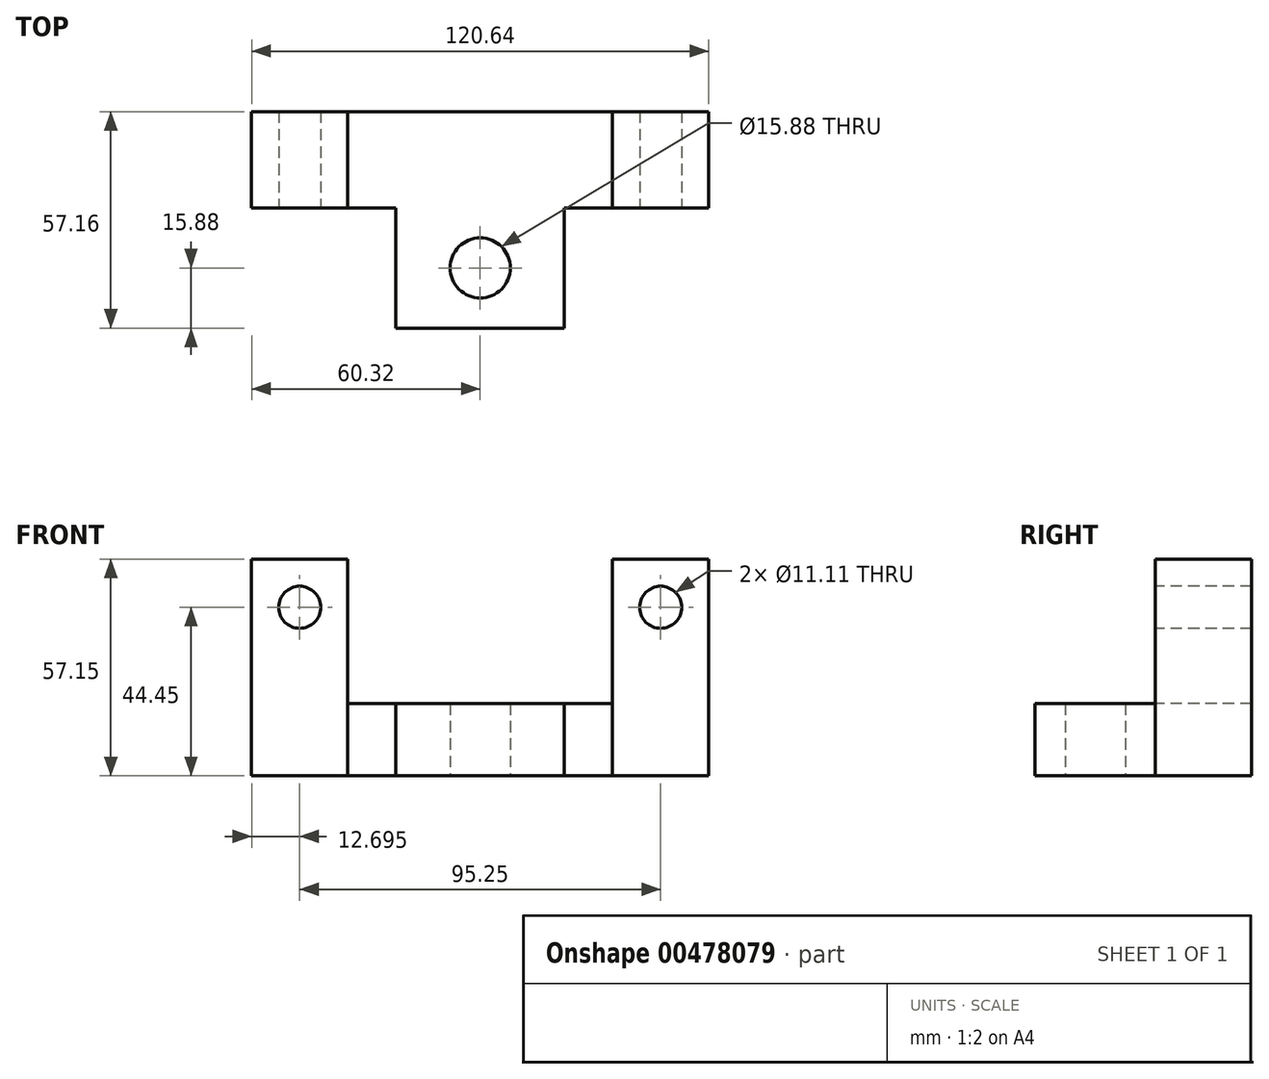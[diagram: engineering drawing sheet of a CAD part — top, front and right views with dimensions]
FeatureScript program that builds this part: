
annotation { "Feature Type Name" : "Feature", "Feature Type Description" : "" }
export const myFeature = defineFeature(function(context is Context, id is Id, definition is map)
    precondition{}
    {
        {
            var Q0;
            Q0=qCreatedBy(makeId("Top.planeOp"),FACE);
            var sketch = newSketch(context, id + "F0", { "sketchPlane" : qUnion([Q0])});
            skCircle(sketch, "E0", {"center": v(0, 0) * mm, "radius": 7.94 * mm});
            skLineSegment(sketch, "E1", {"start": v(-22.23, -15.88) * mm, "end": v(-22.23, 15.87) * mm});
            skLineSegment(sketch, "E2", {"start": v(-22.23, -15.88) * mm, "end": v(0, -15.88) * mm});
            skLineSegment(sketch, "E3", {"start": v(0, -15.88) * mm, "end": v(0, 15.87) * mm});
            skLineSegment(sketch, "E4", {"start": v(0, 15.87) * mm, "end": v(0, 41.28) * mm});
            skLineSegment(sketch, "E5", {"start": v(0, 41.28) * mm, "end": v(-34.93, 41.28) * mm});
            skLineSegment(sketch, "E6", {"start": v(-34.93, 41.28) * mm, "end": v(-34.93, 15.87) * mm});
            skLineSegment(sketch, "E7", {"start": v(-34.93, 15.87) * mm, "end": v(-22.23, 15.87) * mm});
            skLineSegment(sketch, "E8", {"start": v(-34.93, 41.28) * mm, "end": v(-60.32, 41.28) * mm});
            skLineSegment(sketch, "E9", {"start": v(-60.32, 41.27) * mm, "end": v(-60.32, 15.87) * mm});
            skLineSegment(sketch, "E10", {"start": v(-60.32, 15.87) * mm, "end": v(-34.93, 15.87) * mm});
            skLineSegment(sketch, "E11.MirrorCS", {"start": v(22.23, -15.88) * mm, "end": v(22.23, 15.87) * mm});
            skLineSegment(sketch, "E12.MirrorCS", {"start": v(60.32, 15.87) * mm, "end": v(34.93, 15.87) * mm});
            skLineSegment(sketch, "E13.MirrorCS", {"start": v(22.23, -15.88) * mm, "end": v(0, -15.88) * mm});
            skLineSegment(sketch, "E14.MirrorCS", {"start": v(60.32, 41.27) * mm, "end": v(60.32, 15.87) * mm});
            skLineSegment(sketch, "E15.MirrorCS", {"start": v(34.93, 15.87) * mm, "end": v(22.23, 15.87) * mm});
            skLineSegment(sketch, "E16.MirrorCS", {"start": v(34.93, 41.28) * mm, "end": v(60.32, 41.28) * mm});
            skLineSegment(sketch, "E17.MirrorCS", {"start": v(0, 41.28) * mm, "end": v(34.93, 41.28) * mm});
            skLineSegment(sketch, "E18.MirrorCS", {"start": v(34.93, 41.28) * mm, "end": v(34.93, 15.87) * mm});
            skSolve(sketch);
        }
        {
            var Q0;
            Q0=makeQuery(id+"F0.imprint","IMPRINT",FACE,{"disambiguationData":[TD([[makeQuery(id+"F0.imprint","IMPRINT",EDGE,{"derivedFrom":sQuery(id+"F0.wireOp",EDGE,"E8")}),1.0]])]});
            extrude(context, id + "F1", {"entities" : qUnion([Q0]), "depth" : 57.15 * mm});
        }
        {
            var Q0;
            Q0=makeQuery(id+"F0.imprint","IMPRINT",FACE,{"disambiguationData":[TD([[makeQuery(id+"F0.imprint","IMPRINT",EDGE,{"derivedFrom":sQuery(id+"F0.wireOp",EDGE,"E12.MirrorCS")}),-1.0]])]});
            extrude(context, id + "F2", {"entities" : qUnion([Q0]), "depth" : 57.15 * mm});
        }
        {
            var Q0;
            Q0=makeQuery(id+"F0.imprint","IMPRINT",FACE,{"disambiguationData":[TD([[makeQuery(id+"F0.imprint","IMPRINT",EDGE,{"derivedFrom":sQuery(id+"F0.wireOp",EDGE,"E1")}),-1.0]])]});
            var Q1;
            {var subQ5=sQuery(id+"F0.wireOp",EDGE,"E4");Q1=makeQuery(id+"F0.imprint","IMPRINT",FACE,{"disambiguationData":[TD([[makeQuery(id+"F0.imprint","IMPRINT",EDGE,{"derivedFrom":subQ5}),-1.0]])]});}
            extrude(context, id + "F3", {"entities" : qUnion([Q0, Q1]), "depth" : 19.05 * mm});
        }
        {
            var Q0;
            Q0=qCreatedBy(makeId("Front.planeOp"),FACE);
            var sketch = newSketch(context, id + "F4", { "sketchPlane" : qUnion([Q0])});
            skLineSegment(sketch, "E19", {"start": v(0, 0) * mm, "end": v(-47.62, 0) * mm});
            skLineSegment(sketch, "E20", {"start": v(-47.62, 0) * mm, "end": v(-47.62, 44.45) * mm});
            skCircle(sketch, "E21", {"center": v(-47.62, 44.45) * mm, "radius": 5.56 * mm});
            skLineSegment(sketch, "E22", {"start": v(0, 0) * mm, "end": v(47.63, 0) * mm});
            skLineSegment(sketch, "E23", {"start": v(47.63, 0) * mm, "end": v(47.63, 44.45) * mm});
            skCircle(sketch, "E24", {"center": v(47.63, 44.45) * mm, "radius": 5.56 * mm});
            skSolve(sketch);
        }
        {
            var Q0;
            Q0 = qSketchRegion(id + "F4", true);
            extrude(context, id + "F5", {"entities" : qUnion([Q0]), "operationType" : NewBodyOperationType.REMOVE, "oppositeDirection" : true, "depth" : 49.02 * mm});
        }
        {
            var Q0;
            Q0 = qSketchRegion(id + "F4", true);
            extrude(context, id + "F6", {"entities" : qUnion([Q0]), "operationType" : NewBodyOperationType.REMOVE, "oppositeDirection" : true, "depth" : 48.77 * mm});
        }
    });
